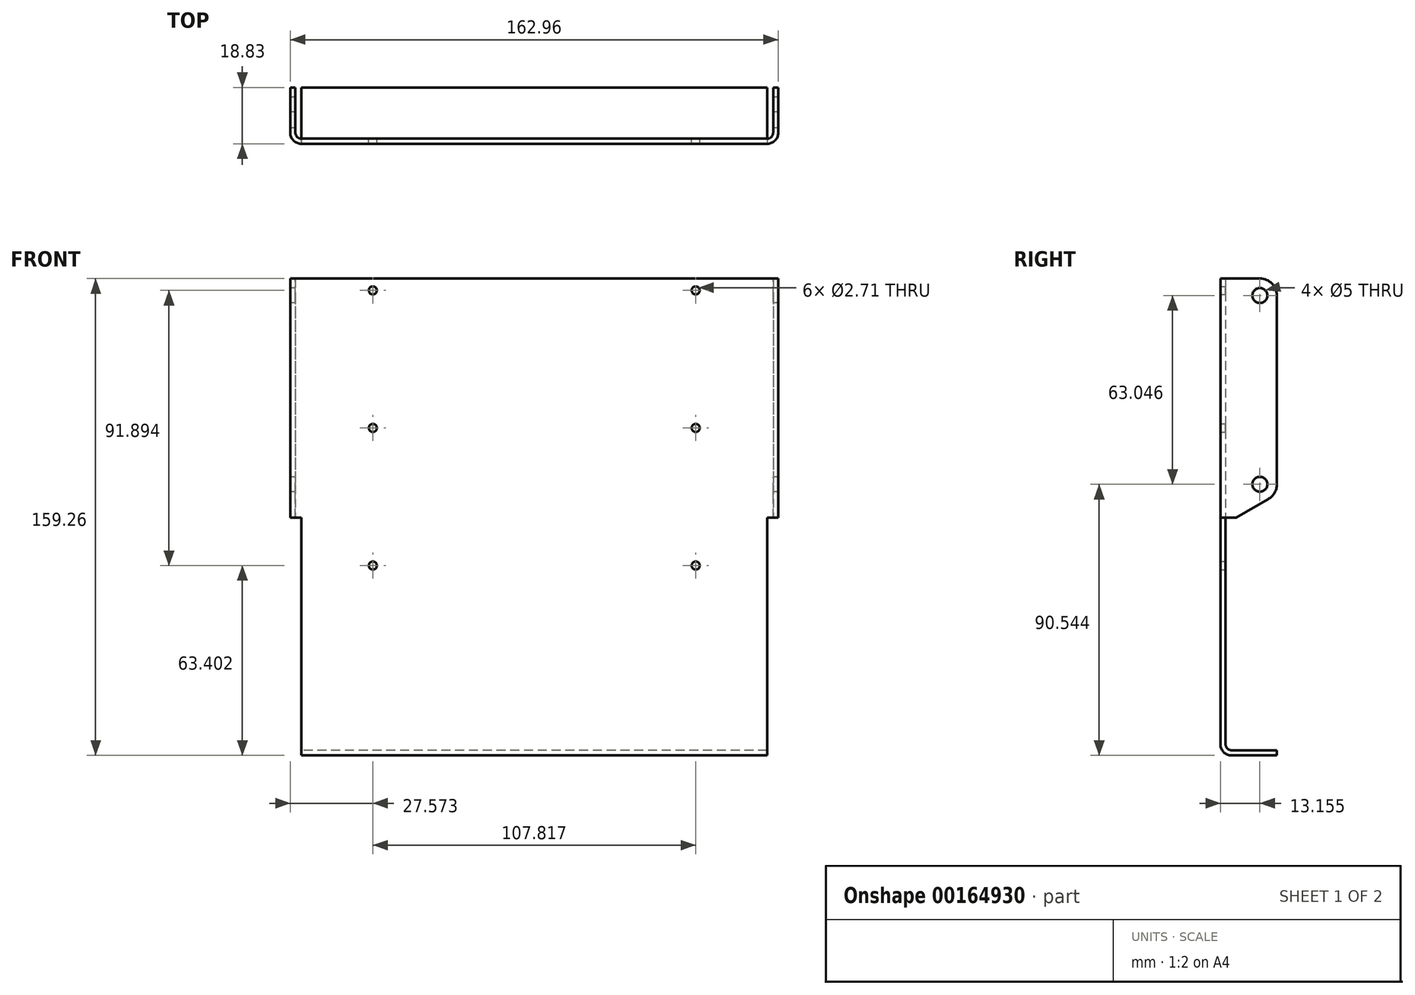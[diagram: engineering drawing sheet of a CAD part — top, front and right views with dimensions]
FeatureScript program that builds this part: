
annotation { "Feature Type Name" : "Feature", "Feature Type Description" : "" }
export const myFeature = defineFeature(function(context is Context, id is Id, definition is map)
    precondition{}
    {
        {
            var Q0;
            Q0=qCreatedBy(makeId("Top.planeOp"),FACE);
            var sketch = newSketch(context, id + "F0", { "sketchPlane" : qUnion([Q0])});
            skLineSegment(sketch, "E0", {"start": v(-1.7, 0) * mm, "end": v(0, 0) * mm});
            skLineSegment(sketch, "E1", {"start": v(-1.7, -18.83) * mm, "end": v(-1.7, 0) * mm});
            skLineSegment(sketch, "E2", {"start": v(159.54, 0) * mm, "end": v(161.25, 0) * mm});
            skLineSegment(sketch, "E3", {"start": v(161.25, 0) * mm, "end": v(161.25, -18.83) * mm});
            skLineSegment(sketch, "E4", {"start": v(-1.7, -18.83) * mm, "end": v(161.25, -18.83) * mm});
            skLineSegment(sketch, "E5", {"start": v(79.77, -18.83) * mm, "end": v(79.77, -17.12) * mm, "construction": true});
            skLineSegment(sketch, "E6.bottom", {"start": v(159.54, 0) * mm, "end": v(0, 0) * mm, "construction": true});
            skLineSegment(sketch, "E6.top", {"start": v(159.54, -17.12) * mm, "end": v(0, -17.12) * mm});
            skLineSegment(sketch, "E6.left", {"start": v(159.54, 0) * mm, "end": v(159.54, -17.12) * mm});
            skLineSegment(sketch, "E6.right", {"start": v(0, 0) * mm, "end": v(0, -17.12) * mm});
            skSolve(sketch);
        }
        {
            var Q0;
            Q0=qSketchRegion(id+"F0",true);
            extrude(context, id + "F1", {"entities" : qUnion([Q0]), "depth" : 155.57 * mm});
        }
        {
            var Q0;
            Q0=makeQuery(id+"F1.opExtrude","SWEPT_EDGE",EDGE,{"disambiguationData":[OSD([sQuery(id+"F0.wireOp",EDGE,"E3"),sQuery(id+"F0.wireOp",EDGE,"E4")])]});
            var Q1;
            Q1=makeQuery(id+"F1.opExtrude","SWEPT_EDGE",EDGE,{"disambiguationData":[OSD([sQuery(id+"F0.wireOp",EDGE,"E1"),sQuery(id+"F0.wireOp",EDGE,"E4")])]});
            var Q2;
            Q2=makeQuery(id+"F1.opExtrude","SWEPT_EDGE",EDGE,{"disambiguationData":[OSD([sQuery(id+"F0.wireOp",EDGE,"E1"),sQuery(id+"F0.wireOp",EDGE,"E4")])]});
            var Q3;
            Q3=makeQuery(id+"F1.opExtrude","SWEPT_EDGE",EDGE,{"disambiguationData":[OSD([sQuery(id+"F0.wireOp",EDGE,"E3"),sQuery(id+"F0.wireOp",EDGE,"E4")])]});
            fillet(context, id + "F2", {"entities" : qUnion([Q0, Q1, Q2, Q3]), "radius" : 3.7 * mm, "tangentPropagation" : true, "allowEdgeOverflow" : false});
        }
        {
            var Q0;
            Q0=makeQuery(id+"F1.opExtrude","SWEPT_EDGE",EDGE,{"disambiguationData":[OSD([sQuery(id+"F0.wireOp",EDGE,"E6.top"),sQuery(id+"F0.wireOp",EDGE,"E6.left")])]});
            var Q1;
            Q1=makeQuery(id+"F1.opExtrude","SWEPT_EDGE",EDGE,{"disambiguationData":[OSD([sQuery(id+"F0.wireOp",EDGE,"E6.top"),sQuery(id+"F0.wireOp",EDGE,"E6.right")])]});
            fillet(context, id + "F3", {"entities" : qUnion([Q0, Q1]), "radius" : 1.98 * mm, "tangentPropagation" : true, "allowEdgeOverflow" : false});
        }
        {
            var Q0;
            Q0=makeQuery(id+"F1.opExtrude","SWEPT_FACE",FACE,{"disambiguationData":[OSD([sQuery(id+"F0.wireOp",EDGE,"E6.right")])]});
            cPlane(context, id + "F4", {"entities" : qUnion([Q0]), "cplaneType" : CPlaneType.OFFSET, "offset" : 1.98 * mm, "width" : 152.4 * mm, "height" : 152.4 * mm});
        }
        {
            var Q0;
            Q0=qCreatedBy(id+"F4.planeOp",FACE);
            var sketch = newSketch(context, id + "F5", { "sketchPlane" : qUnion([Q0])});
            skArc(sketch, "E7", {"start": v(-18.83, 0) * mm, "mid": v(-17.74, -2.61) * mm, "end": v(-15.13, -3.7) * mm});
            skArc(sketch, "E8", {"start": v(-17.12, 0) * mm, "mid": v(-16.54, -1.4) * mm, "end": v(-15.13, -1.98) * mm});
            skLineSegment(sketch, "E9", {"start": v(-18.83, 0) * mm, "end": v(-17.12, 0) * mm});
            skLineSegment(sketch, "E10.bottom", {"start": v(-15.13, -1.98) * mm, "end": v(0, -1.98) * mm});
            skLineSegment(sketch, "E10.top", {"start": v(-15.13, -3.7) * mm, "end": v(0, -3.7) * mm});
            skLineSegment(sketch, "E10.left", {"start": v(-15.13, -1.98) * mm, "end": v(-15.13, -3.7) * mm, "construction": true});
            skLineSegment(sketch, "E10.right", {"start": v(0, -1.98) * mm, "end": v(0, -3.7) * mm});
            skSolve(sketch);
        }
        {
            var Q0;
            Q0=makeQuery(id+"F1.opExtrude","SWEPT_FACE",FACE,{"disambiguationData":[OSD([sQuery(id+"F0.wireOp",EDGE,"E6.left")])]});
            cPlane(context, id + "F6", {"entities" : qUnion([Q0]), "cplaneType" : CPlaneType.OFFSET, "offset" : 1.98 * mm, "width" : 152.4 * mm, "height" : 152.4 * mm});
        }
        {
            var Q0;
            Q0=qSketchRegion(id+"F5",true);
            var Q1;
            Q1=qCreatedBy(id+"F6.planeOp",FACE);
            extrude(context, id + "F7", {"entities" : qUnion([Q0]), "operationType" : NewBodyOperationType.ADD, "endBound" : BoundingType.UP_TO_SURFACE, "endBoundEntityFace" : qUnion([Q1]), "depth" : 25.4 * mm});
        }
        {
            var Q0;
            Q0=makeQuery(id+"F1.opExtrude","SWEPT_FACE",FACE,{"disambiguationData":[OSD([sQuery(id+"F0.wireOp",EDGE,"E1")])]});
            var sketch = newSketch(context, id + "F8", { "sketchPlane" : qUnion([Q0])});
            skLineSegment(sketch, "E11.bottom", {"start": v(0, 155.58) * mm, "end": v(5.67, 155.58) * mm, "construction": true});
            skLineSegment(sketch, "E11.top", {"start": v(0, 149.9) * mm, "end": v(5.68, 149.9) * mm, "construction": true});
            skLineSegment(sketch, "E11.left", {"start": v(0, 155.58) * mm, "end": v(0, 149.9) * mm, "construction": true});
            skLineSegment(sketch, "E11.right", {"start": v(5.67, 155.58) * mm, "end": v(5.67, 149.9) * mm, "construction": true});
            skLineSegment(sketch, "E12", {"start": v(5.68, 149.9) * mm, "end": v(5.68, 86.85) * mm, "construction": true});
            skLineSegment(sketch, "E13", {"start": v(5.68, 86.85) * mm, "end": v(5.68, 0) * mm, "construction": true});
            skCircle(sketch, "E14", {"center": v(5.68, 149.9) * mm, "radius": 2.5 * mm});
            skCircle(sketch, "E15", {"center": v(5.68, 86.85) * mm, "radius": 2.5 * mm});
            skArc(sketch, "E16", {"start": v(0, 86.85) * mm, "mid": v(0.76, 84.02) * mm, "end": v(2.84, 81.94) * mm});
            skLineSegment(sketch, "E17", {"start": v(2.84, 81.94) * mm, "end": v(13.55, 75.76) * mm});
            skLineSegment(sketch, "E18", {"start": v(13.55, 75.76) * mm, "end": v(15.13, 75.76) * mm});
            skLineSegment(sketch, "E19.top", {"start": v(15.13, 0) * mm, "end": v(0, 0) * mm});
            skLineSegment(sketch, "E19.left", {"start": v(15.13, 75.76) * mm, "end": v(15.13, 0) * mm});
            skLineSegment(sketch, "E19.right", {"start": v(0, 86.85) * mm, "end": v(0, 0) * mm});
            skSolve(sketch);
        }
        {
            var Q0;
            Q0=qSketchRegion(id+"F8",true);
            var Q1;
            Q1=makeQuery(id+"F1.opExtrude","SWEPT_FACE",FACE,{"disambiguationData":[OSD([sQuery(id+"F0.wireOp",EDGE,"E3")])]});
            extrude(context, id + "F9", {"entities" : qUnion([Q0]), "operationType" : NewBodyOperationType.REMOVE, "endBound" : BoundingType.UP_TO_SURFACE, "oppositeDirection" : true, "endBoundEntityFace" : qUnion([Q1]), "depth" : 25.4 * mm});
        }
        {
            var Q0;
            Q0=makeQuery(id+"F1.opExtrude","CAP_EDGE",EDGE,{"disambiguationData":[OSD([sQuery(id+"F0.wireOp",EDGE,"E0")])],"isStart":false});
            var Q1;
            Q1=makeQuery(id+"F1.opExtrude","CAP_EDGE",EDGE,{"disambiguationData":[OSD([sQuery(id+"F0.wireOp",EDGE,"E2")])],"isStart":false});
            fillet(context, id + "F10", {"entities" : qUnion([Q0, Q1]), "radius" : 5.67 * mm, "tangentPropagation" : true, "allowEdgeOverflow" : false});
        }
        {
            var Q0;
            Q0=makeQuery(id+"F1.opExtrude","SWEPT_FACE",FACE,{"disambiguationData":[OSD([sQuery(id+"F0.wireOp",EDGE,"E6.top")])]});
            var sketch = newSketch(context, id + "F11", { "sketchPlane" : qUnion([Q0])});
            skLineSegment(sketch, "E20", {"start": v(-79.77, 155.58) * mm, "end": v(-79.77, 105.66) * mm, "construction": true});
            skLineSegment(sketch, "E21.bottom", {"start": v(-25.86, 151.6) * mm, "end": v(-133.68, 151.6) * mm, "construction": true});
            skLineSegment(sketch, "E21.top", {"start": v(-25.86, 59.71) * mm, "end": v(-133.68, 59.71) * mm, "construction": true});
            skLineSegment(sketch, "E21.left", {"start": v(-25.86, 151.6) * mm, "end": v(-25.86, 59.71) * mm, "construction": true});
            skLineSegment(sketch, "E21.right", {"start": v(-133.68, 151.6) * mm, "end": v(-133.68, 59.71) * mm, "construction": true});
            skPoint(sketch, "E21.middle", {"position": v(-79.77, 105.66) * mm});
            skLineSegment(sketch, "E22", {"start": v(-25.86, 151.6) * mm, "end": v(-25.86, 155.58) * mm, "construction": true});
            skCircle(sketch, "E23", {"center": v(-25.86, 59.71) * mm, "radius": 1.35 * mm});
            skCircle(sketch, "E24", {"center": v(-25.86, 105.66) * mm, "radius": 1.35 * mm});
            skCircle(sketch, "E25", {"center": v(-25.86, 151.6) * mm, "radius": 1.35 * mm});
            skCircle(sketch, "E26", {"center": v(-133.68, 151.6) * mm, "radius": 1.35 * mm});
            skCircle(sketch, "E27", {"center": v(-133.68, 105.66) * mm, "radius": 1.35 * mm});
            skCircle(sketch, "E28", {"center": v(-133.68, 59.71) * mm, "radius": 1.35 * mm});
            skSolve(sketch);
        }
        {
            var Q0;
            Q0=qSketchRegion(id+"F11",true);
            var Q1;
            Q1=makeQuery(id+"F1.opExtrude","SWEPT_FACE",FACE,{"disambiguationData":[OSD([sQuery(id+"F0.wireOp",EDGE,"E4")])]});
            extrude(context, id + "F12", {"entities" : qUnion([Q0]), "operationType" : NewBodyOperationType.REMOVE, "endBound" : BoundingType.UP_TO_SURFACE, "oppositeDirection" : true, "endBoundEntityFace" : qUnion([Q1]), "depth" : 25.4 * mm});
        }
        {
            var Q0;
            Q0=makeQuery(id+"F1.opExtrude","SWEPT_FACE",FACE,{"disambiguationData":[OSD([sQuery(id+"F0.wireOp",EDGE,"E4")])]});
            var sketch = newSketch(context, id + "F13", { "sketchPlane" : qUnion([Q0])});
            skLineSegment(sketch, "E29.bottom", {"start": v(1.98, 0) * mm, "end": v(-1.7, 0) * mm});
            skLineSegment(sketch, "E29.top", {"start": v(1.98, 75.76) * mm, "end": v(-1.7, 75.76) * mm});
            skLineSegment(sketch, "E29.left", {"start": v(1.98, 0) * mm, "end": v(1.98, 75.76) * mm});
            skLineSegment(sketch, "E29.right", {"start": v(-1.7, 0) * mm, "end": v(-1.7, 75.76) * mm});
            skLineSegment(sketch, "E30.bottom", {"start": v(157.56, 0) * mm, "end": v(161.25, 0) * mm});
            skLineSegment(sketch, "E30.top", {"start": v(157.56, 75.76) * mm, "end": v(161.25, 75.76) * mm});
            skLineSegment(sketch, "E30.left", {"start": v(157.56, 0) * mm, "end": v(157.56, 75.76) * mm});
            skLineSegment(sketch, "E30.right", {"start": v(161.25, 0) * mm, "end": v(161.25, 75.76) * mm});
            skSolve(sketch);
        }
        {
            var Q0;
            Q0=qSketchRegion(id+"F13",true);
            var Q1;
            {var subQ1=sQuery(id+"F0.wireOp",EDGE,"E1");Q1=makeQuery(id+"F9.boolean.opBoolean","COPY",FACE,{"disambiguationData":[TD([makeQuery(id+"F1.opExtrude","SWEPT_FACE",FACE,{"disambiguationData":[OSD([subQ1])]})])],"derivedFrom":makeQuery(id+"F9.opExtrude","SWEPT_FACE",FACE,{"disambiguationData":[OSD([sQuery(id+"F8.wireOp",EDGE,"E19.left")])]})});}
            extrude(context, id + "F14", {"entities" : qUnion([Q0]), "operationType" : NewBodyOperationType.REMOVE, "endBound" : BoundingType.UP_TO_SURFACE, "oppositeDirection" : true, "endBoundEntityFace" : qUnion([Q1]), "depth" : 25.4 * mm});
        }
    });
